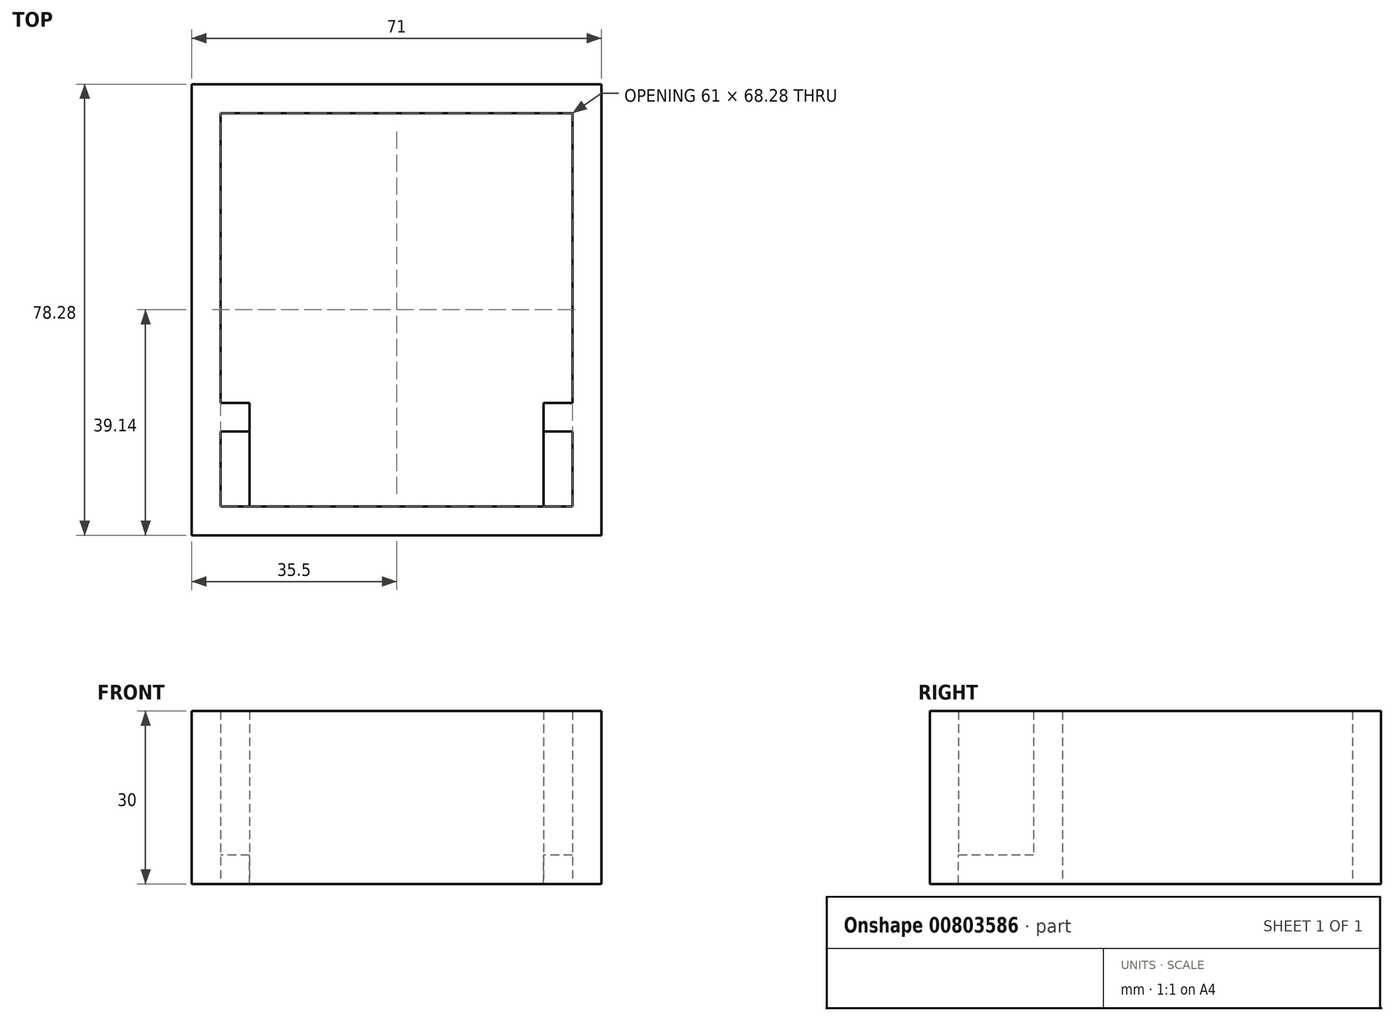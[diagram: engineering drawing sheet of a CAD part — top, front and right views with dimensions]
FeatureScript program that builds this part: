
annotation { "Feature Type Name" : "Feature", "Feature Type Description" : "" }
export const myFeature = defineFeature(function(context is Context, id is Id, definition is map)
    precondition{}
    {
        {
            var Q0;
            Q0=qCreatedBy(makeId("Top.planeOp"),FACE);
            var sketch = newSketch(context, id + "F0", { "sketchPlane" : qUnion([Q0])});
            skPoint(sketch, "E0.middle", {"position": v(0, 0) * mm});
            skLineSegment(sketch, "E1.bottom", {"start": v(35.5, -39.14) * mm, "end": v(-35.5, -39.14) * mm});
            skLineSegment(sketch, "E1.top", {"start": v(35.5, 39.14) * mm, "end": v(-35.5, 39.14) * mm});
            skLineSegment(sketch, "E1.left", {"start": v(35.5, -39.14) * mm, "end": v(35.5, 39.14) * mm});
            skLineSegment(sketch, "E1.right", {"start": v(-35.5, -39.14) * mm, "end": v(-35.5, 39.14) * mm});
            skLineSegment(sketch, "E2", {"start": v(-30.5, -21.14) * mm, "end": v(-30.5, -34.14) * mm});
            skLineSegment(sketch, "E3", {"start": v(-30.5, -34.14) * mm, "end": v(30.5, -34.14) * mm});
            skLineSegment(sketch, "E4", {"start": v(30.5, -34.14) * mm, "end": v(30.5, -21.14) * mm});
            skLineSegment(sketch, "E5", {"start": v(30.5, -21.14) * mm, "end": v(25.5, -21.14) * mm});
            skLineSegment(sketch, "E6", {"start": v(30.5, 34.14) * mm, "end": v(-30.5, 34.14) * mm});
            skLineSegment(sketch, "E7", {"start": v(-25.5, -21.14) * mm, "end": v(-30.5, -21.14) * mm});
            skLineSegment(sketch, "E8", {"start": v(-25.5, -21.14) * mm, "end": v(-25.5, -16.14) * mm});
            skLineSegment(sketch, "E9", {"start": v(-25.5, -16.14) * mm, "end": v(-30.5, -16.14) * mm});
            skLineSegment(sketch, "E10", {"start": v(-30.5, -16.14) * mm, "end": v(-30.5, 34.14) * mm});
            skLineSegment(sketch, "E11", {"start": v(25.5, -21.14) * mm, "end": v(25.5, -16.14) * mm});
            skLineSegment(sketch, "E12", {"start": v(25.5, -16.14) * mm, "end": v(30.5, -16.14) * mm});
            skLineSegment(sketch, "E13", {"start": v(30.5, -16.14) * mm, "end": v(30.5, 34.14) * mm});
            skSolve(sketch);
        }
        {
            var Q0;
            Q0 = qSketchRegion(id + "F0", true);
            extrude(context, id + "F1", {"entities" : qUnion([Q0]), "depth" : 25 * mm, "offsetDistance" : 25 * mm});
        }
        {
            var Q0;
            Q0=makeQuery(id+"F1.opExtrude","CAP_FACE",FACE,{"disambiguationData":[OSD([sQuery(id+"F0.wireOp",EDGE,"E1.bottom"),sQuery(id+"F0.wireOp",EDGE,"E1.top"),sQuery(id+"F0.wireOp",EDGE,"E1.left"),sQuery(id+"F0.wireOp",EDGE,"E1.right"),sQuery(id+"F0.wireOp",EDGE,"E2"),sQuery(id+"F0.wireOp",EDGE,"E3"),sQuery(id+"F0.wireOp",EDGE,"E4"),sQuery(id+"F0.wireOp",EDGE,"E5"),sQuery(id+"F0.wireOp",EDGE,"E6"),sQuery(id+"F0.wireOp",EDGE,"E7"),sQuery(id+"F0.wireOp",EDGE,"E8"),sQuery(id+"F0.wireOp",EDGE,"E9"),sQuery(id+"F0.wireOp",EDGE,"E10"),sQuery(id+"F0.wireOp",EDGE,"E11"),sQuery(id+"F0.wireOp",EDGE,"E12"),sQuery(id+"F0.wireOp",EDGE,"E13")])],"isStart":true});
            var sketch = newSketch(context, id + "F2", { "sketchPlane" : qUnion([Q0])});
            skLineSegment(sketch, "E14", {"start": v(25.5, 34.14) * mm, "end": v(25.5, 16.14) * mm});
            skLineSegment(sketch, "E15", {"start": v(25.5, 16.14) * mm, "end": v(30.5, 16.14) * mm});
            skLineSegment(sketch, "E16", {"start": v(30.5, 16.14) * mm, "end": v(30.5, -34.14) * mm});
            skLineSegment(sketch, "E17", {"start": v(30.5, -34.14) * mm, "end": v(-30.5, -34.14) * mm});
            skLineSegment(sketch, "E18", {"start": v(-30.5, -34.14) * mm, "end": v(-30.5, 16.14) * mm});
            skLineSegment(sketch, "E19", {"start": v(-30.5, 16.14) * mm, "end": v(-25.5, 16.14) * mm});
            skLineSegment(sketch, "E20", {"start": v(-25.5, 16.14) * mm, "end": v(-25.5, 34.14) * mm});
            skLineSegment(sketch, "E21", {"start": v(-25.5, 34.14) * mm, "end": v(25.5, 34.14) * mm});
            skLineSegment(sketch, "E22.bottom", {"start": v(-35.5, 39.14) * mm, "end": v(35.5, 39.14) * mm});
            skLineSegment(sketch, "E22.top", {"start": v(-35.5, -39.14) * mm, "end": v(35.5, -39.14) * mm});
            skLineSegment(sketch, "E22.left", {"start": v(-35.5, 39.14) * mm, "end": v(-35.5, -39.14) * mm});
            skLineSegment(sketch, "E22.right", {"start": v(35.5, 39.14) * mm, "end": v(35.5, -39.14) * mm});
            skSolve(sketch);
        }
        {
            var Q0;
            Q0 = qSketchRegion(id + "F2", true);
            extrude(context, id + "F3", {"entities" : qUnion([Q0]), "operationType" : NewBodyOperationType.ADD, "depth" : 5 * mm, "offsetDistance" : 25 * mm});
        }
    });
